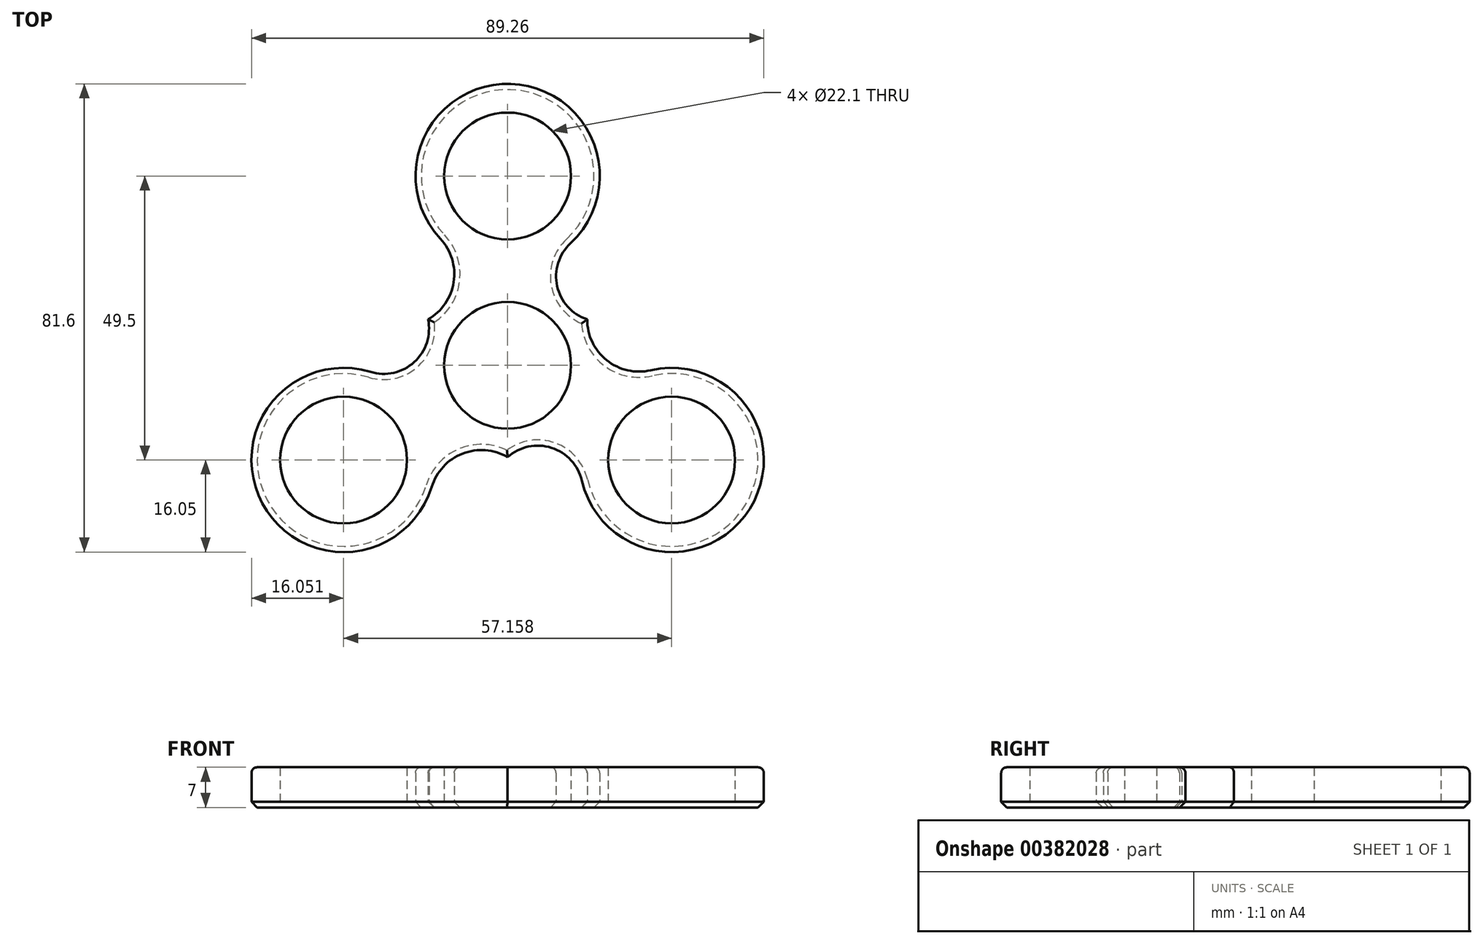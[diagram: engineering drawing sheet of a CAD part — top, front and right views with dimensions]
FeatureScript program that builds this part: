
annotation { "Feature Type Name" : "Feature", "Feature Type Description" : "" }
export const myFeature = defineFeature(function(context is Context, id is Id, definition is map)
    precondition{}
    {
        {
            var Q0;
            Q0=qCreatedBy(makeId("Top.planeOp"),FACE);
            var sketch = newSketch(context, id + "F0", { "sketchPlane" : qUnion([Q0])});
            skLineSegment(sketch, "E0", {"start": v(0, 0) * mm, "end": v(0, 33) * mm, "construction": true});
            skCircle(sketch, "E1", {"center": v(0, 0) * mm, "radius": 11.05 * mm});
            skCircle(sketch, "E2", {"center": v(0, 33) * mm, "radius": 11.05 * mm});
            skLineSegment(sketch, "E3.1.0", {"start": v(0, 0) * mm, "end": v(-28.58, -16.5) * mm, "construction": true});
            skCircle(sketch, "E3.1.1", {"center": v(-28.58, -16.5) * mm, "radius": 11.05 * mm});
            skLineSegment(sketch, "E3.2.0", {"start": v(0, 0) * mm, "end": v(28.58, -16.5) * mm, "construction": true});
            skCircle(sketch, "E3.2.1", {"center": v(28.58, -16.5) * mm, "radius": 11.05 * mm});
            skLineSegment(sketch, "E4", {"start": v(0, 33) * mm, "end": v(-11.73, 22.05) * mm, "construction": true});
            skLineSegment(sketch, "E5", {"start": v(0, 33) * mm, "end": v(10.95, 21.27) * mm, "construction": true});
            skArc(sketch, "E6", {"start": v(10.95, 21.27) * mm, "mid": v(0.55, 49.04) * mm, "end": v(-11.73, 22.05) * mm});
            skArc(sketch, "E7.1.0", {"start": v(-23.9, -1.15) * mm, "mid": v(-42.75, -24.04) * mm, "end": v(-13.23, -21.18) * mm});
            skArc(sketch, "E7.2.0", {"start": v(12.94, -20.12) * mm, "mid": v(42.2, -25) * mm, "end": v(24.96, -0.86) * mm});
            skLineSegment(sketch, "E8.1.0", {"start": v(0, 0) * mm, "end": v(0, -16) * mm});
            skArc(sketch, "E9", {"start": v(-11.73, 22.05) * mm, "mid": v(-9.4, 14.51) * mm, "end": v(-13.86, 8) * mm});
            skArc(sketch, "E10", {"start": v(-23.9, -1.15) * mm, "mid": v(-16.27, 0.57) * mm, "end": v(-13.86, 8) * mm});
            skArc(sketch, "E11", {"start": v(10.95, 21.27) * mm, "mid": v(8.63, 13.8) * mm, "end": v(13.86, 8) * mm});
            skArc(sketch, "E12", {"start": v(24.96, -0.86) * mm, "mid": v(17.26, 0.88) * mm, "end": v(13.86, 8) * mm});
            skArc(sketch, "E13", {"start": v(-13.23, -21.18) * mm, "mid": v(-7.87, -15.4) * mm, "end": v(0, -16) * mm});
            skArc(sketch, "E14", {"start": v(12.94, -20.12) * mm, "mid": v(7.64, -14.37) * mm, "end": v(0, -16) * mm});
            skSolve(sketch);
        }
        {
            var Q0;
            Q0=makeQuery(id+"F0.imprint","IMPRINT",FACE,{"disambiguationData":[TD([[makeQuery(id+"F0.imprint","IMPRINT",EDGE,{"derivedFrom":sQuery(id+"F0.wireOp",EDGE,"E1")}),-1.0]])]});
            extrude(context, id + "F1", {"entities" : qUnion([Q0]), "endBound" : BoundingType.SYMMETRIC, "depth" : 7 * mm});
        }
        {
            var Q0;
            Q0=makeQuery(id+"F1.opExtrude","CAP_EDGE",EDGE,{"disambiguationData":[OSD([sQuery(id+"F0.wireOp",EDGE,"E6")])],"isStart":false});
            var Q1;
            Q1=makeQuery(id+"F1.opExtrude","CAP_EDGE",EDGE,{"disambiguationData":[OSD([sQuery(id+"F0.wireOp",EDGE,"E7.2.0")])],"isStart":false});
            var Q2;
            Q2=makeQuery(id+"F1.opExtrude","CAP_EDGE",EDGE,{"disambiguationData":[OSD([sQuery(id+"F0.wireOp",EDGE,"E12")])],"isStart":false});
            var Q3;
            Q3=makeQuery(id+"F1.opExtrude","CAP_EDGE",EDGE,{"disambiguationData":[OSD([sQuery(id+"F0.wireOp",EDGE,"E11")])],"isStart":false});
            var Q4;
            Q4=makeQuery(id+"F1.opExtrude","CAP_EDGE",EDGE,{"disambiguationData":[OSD([sQuery(id+"F0.wireOp",EDGE,"E9")])],"isStart":false});
            var Q5;
            Q5=makeQuery(id+"F1.opExtrude","CAP_EDGE",EDGE,{"disambiguationData":[OSD([sQuery(id+"F0.wireOp",EDGE,"E10")])],"isStart":false});
            var Q6;
            Q6=makeQuery(id+"F1.opExtrude","CAP_EDGE",EDGE,{"disambiguationData":[OSD([sQuery(id+"F0.wireOp",EDGE,"E7.1.0")])],"isStart":false});
            var Q7;
            Q7=makeQuery(id+"F1.opExtrude","CAP_EDGE",EDGE,{"disambiguationData":[OSD([sQuery(id+"F0.wireOp",EDGE,"E13")])],"isStart":false});
            var Q8;
            Q8=makeQuery(id+"F1.opExtrude","CAP_EDGE",EDGE,{"disambiguationData":[OSD([sQuery(id+"F0.wireOp",EDGE,"E14")])],"isStart":false});
            fillet(context, id + "F2", {"entities" : qUnion([Q0, Q1, Q2, Q3, Q4, Q5, Q6, Q7, Q8]), "radius" : 1 * mm, "tangentPropagation" : true, "allowEdgeOverflow" : false});
        }
        {
            var Q0;
            Q0=makeQuery(id+"F1.opExtrude","CAP_EDGE",EDGE,{"disambiguationData":[OSD([sQuery(id+"F0.wireOp",EDGE,"E6")])],"isStart":true});
            var Q1;
            Q1=makeQuery(id+"F1.opExtrude","CAP_EDGE",EDGE,{"disambiguationData":[OSD([sQuery(id+"F0.wireOp",EDGE,"E9")])],"isStart":true});
            var Q2;
            Q2=makeQuery(id+"F1.opExtrude","CAP_EDGE",EDGE,{"disambiguationData":[OSD([sQuery(id+"F0.wireOp",EDGE,"E10")])],"isStart":true});
            var Q3;
            Q3=makeQuery(id+"F1.opExtrude","CAP_EDGE",EDGE,{"disambiguationData":[OSD([sQuery(id+"F0.wireOp",EDGE,"E7.1.0")])],"isStart":true});
            var Q4;
            Q4=makeQuery(id+"F1.opExtrude","CAP_EDGE",EDGE,{"disambiguationData":[OSD([sQuery(id+"F0.wireOp",EDGE,"E13")])],"isStart":true});
            var Q5;
            Q5=makeQuery(id+"F1.opExtrude","CAP_EDGE",EDGE,{"disambiguationData":[OSD([sQuery(id+"F0.wireOp",EDGE,"E14")])],"isStart":true});
            var Q6;
            Q6=makeQuery(id+"F1.opExtrude","CAP_EDGE",EDGE,{"disambiguationData":[OSD([sQuery(id+"F0.wireOp",EDGE,"E7.2.0")])],"isStart":true});
            var Q7;
            Q7=makeQuery(id+"F1.opExtrude","CAP_EDGE",EDGE,{"disambiguationData":[OSD([sQuery(id+"F0.wireOp",EDGE,"E12")])],"isStart":true});
            var Q8;
            Q8=makeQuery(id+"F1.opExtrude","CAP_EDGE",EDGE,{"disambiguationData":[OSD([sQuery(id+"F0.wireOp",EDGE,"E11")])],"isStart":true});
            chamfer(context, id + "F3", {"entities" : qUnion([Q0, Q1, Q2, Q3, Q4, Q5, Q6, Q7, Q8]), "width" : 1 * mm, "tangentPropagation" : true});
        }
    });
